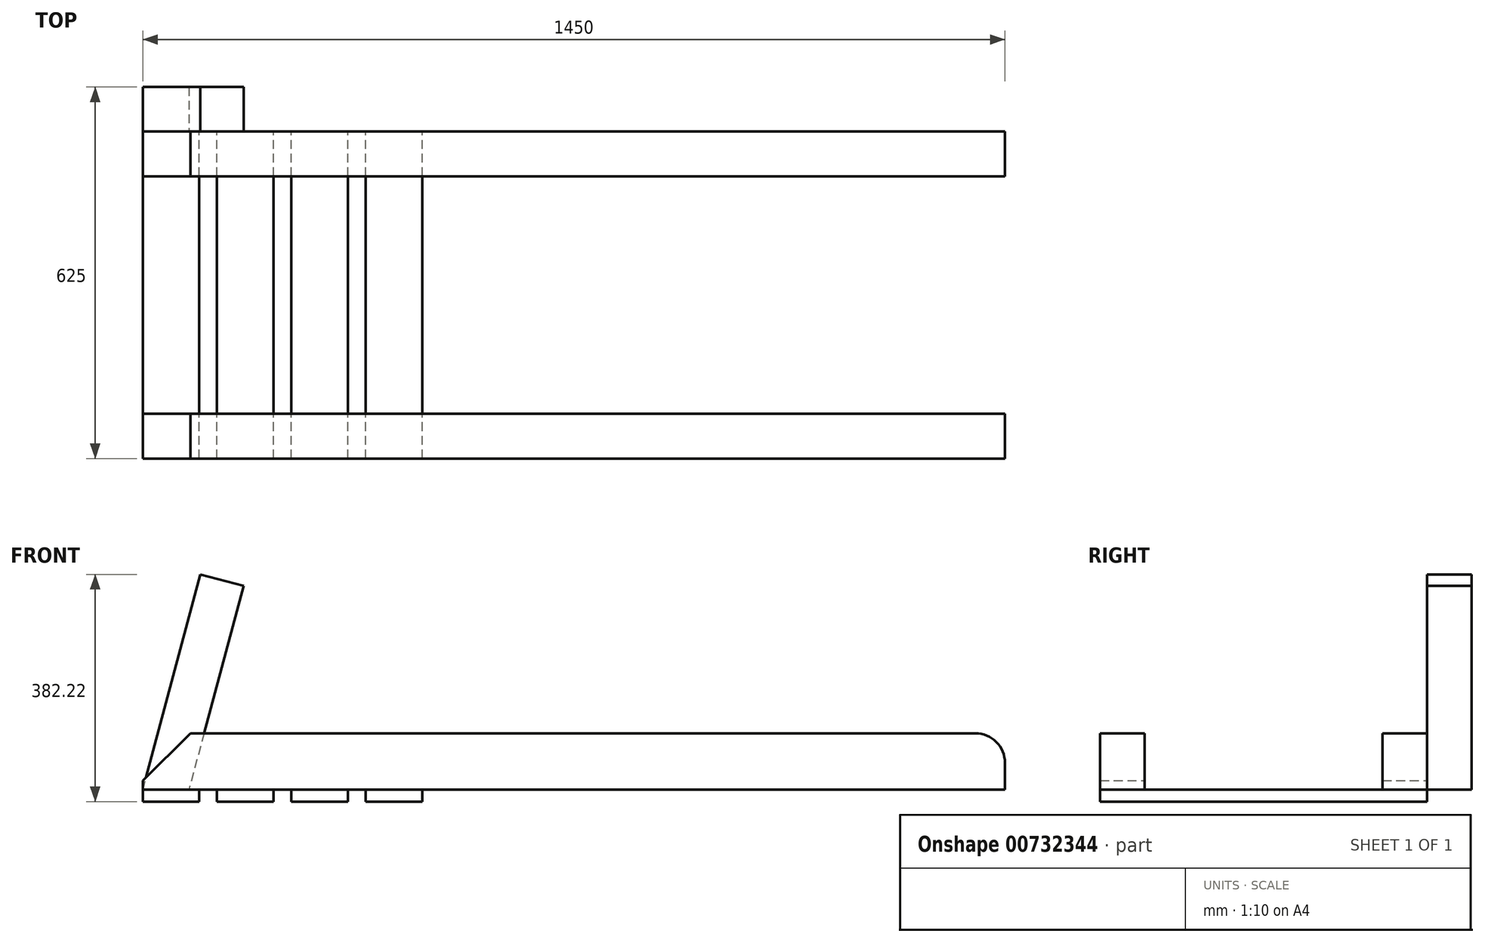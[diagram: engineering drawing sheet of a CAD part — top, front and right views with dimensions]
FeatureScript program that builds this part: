
annotation { "Feature Type Name" : "Feature", "Feature Type Description" : "" }
export const myFeature = defineFeature(function(context is Context, id is Id, definition is map)
    precondition{}
    {
        {
            var Q0;
            Q0=qCreatedBy(makeId("Top.planeOp"),FACE);
            var sketch = newSketch(context, id + "F0", { "sketchPlane" : qUnion([Q0])});
            skLineSegment(sketch, "E0.bottom", {"start": v(-725, 275) * mm, "end": v(725, 275) * mm, "construction": true});
            skLineSegment(sketch, "E0.top", {"start": v(-725, -275) * mm, "end": v(725, -275) * mm, "construction": true});
            skLineSegment(sketch, "E0.left", {"start": v(-725, 275) * mm, "end": v(-725, -275) * mm, "construction": true});
            skLineSegment(sketch, "E0.right", {"start": v(725, 275) * mm, "end": v(725, -275) * mm, "construction": true});
            skPoint(sketch, "E0.middle", {"position": v(0, 0) * mm});
            skLineSegment(sketch, "E1.bottom", {"start": v(-725, 275) * mm, "end": v(725, 275) * mm});
            skLineSegment(sketch, "E1.top", {"start": v(-725, 200) * mm, "end": v(725, 200) * mm});
            skLineSegment(sketch, "E1.left", {"start": v(-725, 275) * mm, "end": v(-725, 200) * mm});
            skLineSegment(sketch, "E1.right", {"start": v(725, 275) * mm, "end": v(725, 200) * mm});
            skLineSegment(sketch, "E2.bottom", {"start": v(-725, -275) * mm, "end": v(725, -275) * mm});
            skLineSegment(sketch, "E2.top", {"start": v(-725, -200) * mm, "end": v(725, -200) * mm});
            skLineSegment(sketch, "E2.left", {"start": v(-725, -275) * mm, "end": v(-725, -200) * mm});
            skLineSegment(sketch, "E2.right", {"start": v(725, -275) * mm, "end": v(725, -200) * mm});
            skSolve(sketch);
        }
        {
            var Q0;
            Q0=makeQuery(id+"F0.imprint","IMPRINT",FACE,{"disambiguationData":[TD([[makeQuery(id+"F0.imprint","IMPRINT",EDGE,{"derivedFrom":sQuery(id+"F0.wireOp",EDGE,"E1.bottom")}),-1.0]])]});
            var Q1;
            Q1=makeQuery(id+"F0.imprint","IMPRINT",FACE,{"disambiguationData":[TD([[makeQuery(id+"F0.imprint","IMPRINT",EDGE,{"derivedFrom":sQuery(id+"F0.wireOp",EDGE,"E2.bottom")}),1.0]])]});
            extrude(context, id + "F1", {"entities" : qUnion([Q0, Q1]), "depth" : 95 * mm, "offsetDistance" : 25 * mm});
        }
        {
            var Q0;
            Q0=qCreatedBy(makeId("Top.planeOp"),FACE);
            var sketch = newSketch(context, id + "F2", { "sketchPlane" : qUnion([Q0])});
            skPoint(sketch, "E3.0", {"position": v(-725, -275) * mm});
            skPoint(sketch, "E4.0", {"position": v(-725, 275) * mm});
            skPoint(sketch, "E5.0", {"position": v(725, -275) * mm});
            skPoint(sketch, "E6.0", {"position": v(725, 275) * mm});
            skLineSegment(sketch, "E7.bottom", {"start": v(-725, -275) * mm, "end": v(-225, -275) * mm, "construction": true});
            skLineSegment(sketch, "E7.top", {"start": v(-725, 275) * mm, "end": v(-225, 275) * mm, "construction": true});
            skLineSegment(sketch, "E7.left", {"start": v(-725, -275) * mm, "end": v(-725, 275) * mm, "construction": true});
            skLineSegment(sketch, "E7.right", {"start": v(-225, -275) * mm, "end": v(-225, 275) * mm, "construction": true});
            skLineSegment(sketch, "E8", {"start": v(-725, -275) * mm, "end": v(-630, -275) * mm, "construction": true});
            skLineSegment(sketch, "E9", {"start": v(-630, -275) * mm, "end": v(-600, -275) * mm, "construction": true});
            skLineSegment(sketch, "E10", {"start": v(-600, -275) * mm, "end": v(-505, -275) * mm, "construction": true});
            skLineSegment(sketch, "E11", {"start": v(-505, -275) * mm, "end": v(-475, -275) * mm, "construction": true});
            skLineSegment(sketch, "E12", {"start": v(-475, -275) * mm, "end": v(-380, -275) * mm, "construction": true});
            skLineSegment(sketch, "E13", {"start": v(-380, -275) * mm, "end": v(-350, -275) * mm, "construction": true});
            skLineSegment(sketch, "E14", {"start": v(-350, -275) * mm, "end": v(-255, -275) * mm, "construction": true});
            skLineSegment(sketch, "E15.bottom", {"start": v(-725, -275) * mm, "end": v(-630, -275) * mm});
            skLineSegment(sketch, "E15.top", {"start": v(-725, 275) * mm, "end": v(-630, 275) * mm});
            skLineSegment(sketch, "E15.left", {"start": v(-725, -275) * mm, "end": v(-725, 275) * mm});
            skLineSegment(sketch, "E15.right", {"start": v(-630, -275) * mm, "end": v(-630, 275) * mm});
            skLineSegment(sketch, "E16.bottom", {"start": v(-600, -275) * mm, "end": v(-505, -275) * mm});
            skLineSegment(sketch, "E16.top", {"start": v(-600, 275) * mm, "end": v(-505, 275) * mm});
            skLineSegment(sketch, "E16.left", {"start": v(-600, -275) * mm, "end": v(-600, 275) * mm});
            skLineSegment(sketch, "E16.right", {"start": v(-505, -275) * mm, "end": v(-505, 275) * mm});
            skLineSegment(sketch, "E17.bottom", {"start": v(-475, -275) * mm, "end": v(-380, -275) * mm});
            skLineSegment(sketch, "E17.top", {"start": v(-475, 275) * mm, "end": v(-380, 275) * mm});
            skLineSegment(sketch, "E17.left", {"start": v(-475, -275) * mm, "end": v(-475, 275) * mm});
            skLineSegment(sketch, "E17.right", {"start": v(-380, -275) * mm, "end": v(-380, 275) * mm});
            skLineSegment(sketch, "E18.bottom", {"start": v(-350, -275) * mm, "end": v(-255, -275) * mm});
            skLineSegment(sketch, "E18.top", {"start": v(-350, 275) * mm, "end": v(-255, 275) * mm});
            skLineSegment(sketch, "E18.left", {"start": v(-350, -275) * mm, "end": v(-350, 275) * mm});
            skLineSegment(sketch, "E18.right", {"start": v(-255, -275) * mm, "end": v(-255, 275) * mm});
            skSolve(sketch);
        }
        {
            var Q0;
            Q0=makeQuery(id+"F2.imprint","IMPRINT",FACE,{"disambiguationData":[TD([[makeQuery(id+"F2.imprint","IMPRINT",EDGE,{"derivedFrom":sQuery(id+"F2.wireOp",EDGE,"E15.bottom")}),1.0]])]});
            var Q1;
            Q1=makeQuery(id+"F2.imprint","IMPRINT",FACE,{"disambiguationData":[TD([[makeQuery(id+"F2.imprint","IMPRINT",EDGE,{"derivedFrom":sQuery(id+"F2.wireOp",EDGE,"E16.bottom")}),1.0]])]});
            var Q2;
            Q2=makeQuery(id+"F2.imprint","IMPRINT",FACE,{"disambiguationData":[TD([[makeQuery(id+"F2.imprint","IMPRINT",EDGE,{"derivedFrom":sQuery(id+"F2.wireOp",EDGE,"E17.bottom")}),1.0]])]});
            var Q3;
            Q3=makeQuery(id+"F2.imprint","IMPRINT",FACE,{"disambiguationData":[TD([[makeQuery(id+"F2.imprint","IMPRINT",EDGE,{"derivedFrom":sQuery(id+"F2.wireOp",EDGE,"E18.bottom")}),1.0]])]});
            extrude(context, id + "F3", {"entities" : qUnion([Q0, Q1, Q2, Q3]), "oppositeDirection" : true, "depth" : 20 * mm, "offsetDistance" : 25 * mm});
        }
        {
            var Q0;
            Q0=makeQuery(id+"F1.opExtrude","CAP_EDGE",EDGE,{"disambiguationData":[OSD([sQuery(id+"F0.wireOp",EDGE,"E1.left")])],"isStart":false});
            var Q1;
            Q1=makeQuery(id+"F1.opExtrude","CAP_EDGE",EDGE,{"disambiguationData":[OSD([sQuery(id+"F0.wireOp",EDGE,"E2.left")])],"isStart":false});
            chamfer(context, id + "F4", {"entities" : qUnion([Q0, Q1]), "width" : 80 * mm, "tangentPropagation" : true});
        }
        {
            var Q0;
            Q0=makeQuery(id+"F1.opExtrude","CAP_EDGE",EDGE,{"disambiguationData":[OSD([sQuery(id+"F0.wireOp",EDGE,"E1.right")])],"isStart":false});
            var Q1;
            Q1=makeQuery(id+"F1.opExtrude","CAP_EDGE",EDGE,{"disambiguationData":[OSD([sQuery(id+"F0.wireOp",EDGE,"E2.right")])],"isStart":false});
            fillet(context, id + "F5", {"entities" : qUnion([Q0, Q1]), "radius" : 50 * mm, "tangentPropagation" : true, "allowEdgeOverflow" : false});
        }
        {
            var Q0;
            Q0=makeQuery(id+"F1.opExtrude","SWEPT_FACE",FACE,{"disambiguationData":[OSD([sQuery(id+"F0.wireOp",EDGE,"E1.bottom")])]});
            var sketch = newSketch(context, id + "F6", { "sketchPlane" : qUnion([Q0])});
            skLineSegment(sketch, "E19.0", {"start": v(725, 0) * mm, "end": v(-725, 0) * mm, "construction": true});
            skLineSegment(sketch, "E20", {"start": v(725, 0) * mm, "end": v(627.94, 362.22) * mm});
            skLineSegment(sketch, "E21", {"start": v(627.94, 362.22) * mm, "end": v(555.5, 342.81) * mm});
            skLineSegment(sketch, "E22", {"start": v(555.5, 342.81) * mm, "end": v(647.35, 0) * mm});
            skLineSegment(sketch, "E23", {"start": v(647.35, 0) * mm, "end": v(725, 0) * mm});
            skLineSegment(sketch, "E24.0", {"start": v(255, -20) * mm, "end": v(255, 0) * mm, "construction": true});
            skSolve(sketch);
        }
        {
            var Q0;
            {var subQ1=sQuery(id+"F6.wireOp",EDGE,"E21");Q0=makeQuery(id+"F6.imprint","IMPRINT",FACE,{"disambiguationData":[TD([[makeQuery(id+"F6.imprint","IMPRINT",EDGE,{"derivedFrom":subQ1}),1.0]])]});}
            var Q1;
            {var subQ7=sQuery(id+"F6.wireOp",EDGE,"E23");Q1=makeQuery(id+"F6.imprint","IMPRINT",FACE,{"disambiguationData":[TD([[makeQuery(id+"F6.imprint","IMPRINT",EDGE,{"derivedFrom":subQ7}),-1.0]])]});}
            extrude(context, id + "F7", {"entities" : qUnion([Q0, Q1]), "depth" : 75 * mm, "offsetDistance" : 25 * mm});
        }
    });
